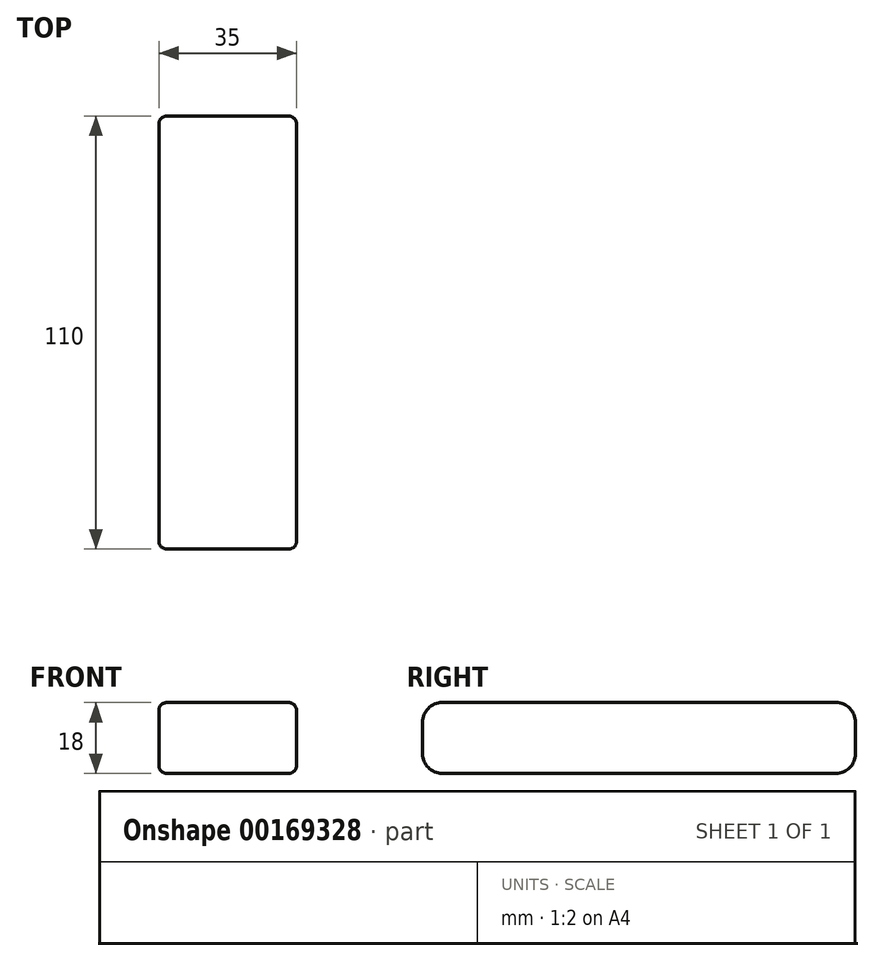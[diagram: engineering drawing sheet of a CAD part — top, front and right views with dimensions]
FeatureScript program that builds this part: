
annotation { "Feature Type Name" : "Feature", "Feature Type Description" : "" }
export const myFeature = defineFeature(function(context is Context, id is Id, definition is map)
    precondition{}
    {
        {
            var Q0;
            Q0=qCreatedBy(makeId("Top.planeOp"),FACE);
            var sketch = newSketch(context, id + "F0", { "sketchPlane" : qUnion([Q0])});
            skLineSegment(sketch, "E0.bottom", {"start": v(17.5, 55) * mm, "end": v(-17.5, 55) * mm});
            skLineSegment(sketch, "E0.top", {"start": v(17.5, -55) * mm, "end": v(-17.5, -55) * mm});
            skLineSegment(sketch, "E0.left", {"start": v(17.5, 55) * mm, "end": v(17.5, -55) * mm});
            skLineSegment(sketch, "E0.right", {"start": v(-17.5, 55) * mm, "end": v(-17.5, -55) * mm});
            skPoint(sketch, "E0.middle", {"position": v(0, 0) * mm});
            skSolve(sketch);
        }
        {
            var Q0;
            Q0=makeQuery(id+"F0.imprint","IMPRINT",FACE,{"disambiguationData":[TD([[makeQuery(id+"F0.imprint","IMPRINT",EDGE,{"derivedFrom":sQuery(id+"F0.wireOp",EDGE,"E0.bottom")}),1.0]])]});
            extrude(context, id + "F1", {"entities" : qUnion([Q0]), "depth" : 18 * mm});
        }
        {
            var Q0;
            Q0=makeQuery(id+"F1.opExtrude","CAP_EDGE",EDGE,{"disambiguationData":[OSD([sQuery(id+"F0.wireOp",EDGE,"E0.bottom")])],"isStart":true});
            var Q1;
            Q1=makeQuery(id+"F1.opExtrude","CAP_EDGE",EDGE,{"disambiguationData":[OSD([sQuery(id+"F0.wireOp",EDGE,"E0.bottom")])],"isStart":false});
            var Q2;
            Q2=makeQuery(id+"F1.opExtrude","CAP_EDGE",EDGE,{"disambiguationData":[OSD([sQuery(id+"F0.wireOp",EDGE,"E0.top")])],"isStart":false});
            var Q3;
            Q3=makeQuery(id+"F1.opExtrude","CAP_EDGE",EDGE,{"disambiguationData":[OSD([sQuery(id+"F0.wireOp",EDGE,"E0.top")])],"isStart":true});
            fillet(context, id + "F2", {"entities" : qUnion([Q0, Q1, Q2, Q3]), "radius" : 5 * mm, "tangentPropagation" : true, "allowEdgeOverflow" : false});
        }
        {
            var Q0;
            Q0=makeQuery(id+"F1.opExtrude","CAP_EDGE",EDGE,{"disambiguationData":[OSD([sQuery(id+"F0.wireOp",EDGE,"E0.right")])],"isStart":false});
            var Q1;
            Q1=makeQuery(id+"F2.opFillet","BLEND_EDGE",EDGE,{"blendedFrom":[makeQuery(id+"F1.opExtrude","CAP_EDGE",EDGE,{"disambiguationData":[OSD([sQuery(id+"F0.wireOp",EDGE,"E0.bottom")])],"isStart":false}),makeQuery(id+"F1.opExtrude","SWEPT_FACE",FACE,{"disambiguationData":[OSD([sQuery(id+"F0.wireOp",EDGE,"E0.right")])]})],"blendedInto":[makeQuery(id+"F1.opExtrude","SWEPT_FACE",FACE,{"disambiguationData":[OSD([sQuery(id+"F0.wireOp",EDGE,"E0.right")])]})]});
            var Q2;
            Q2=makeQuery(id+"F1.opExtrude","CAP_EDGE",EDGE,{"disambiguationData":[OSD([sQuery(id+"F0.wireOp",EDGE,"E0.left")])],"isStart":false});
            fillet(context, id + "F3", {"entities" : qUnion([Q0, Q1, Q2]), "radius" : 2 * mm, "tangentPropagation" : true, "allowEdgeOverflow" : false});
        }
    });
